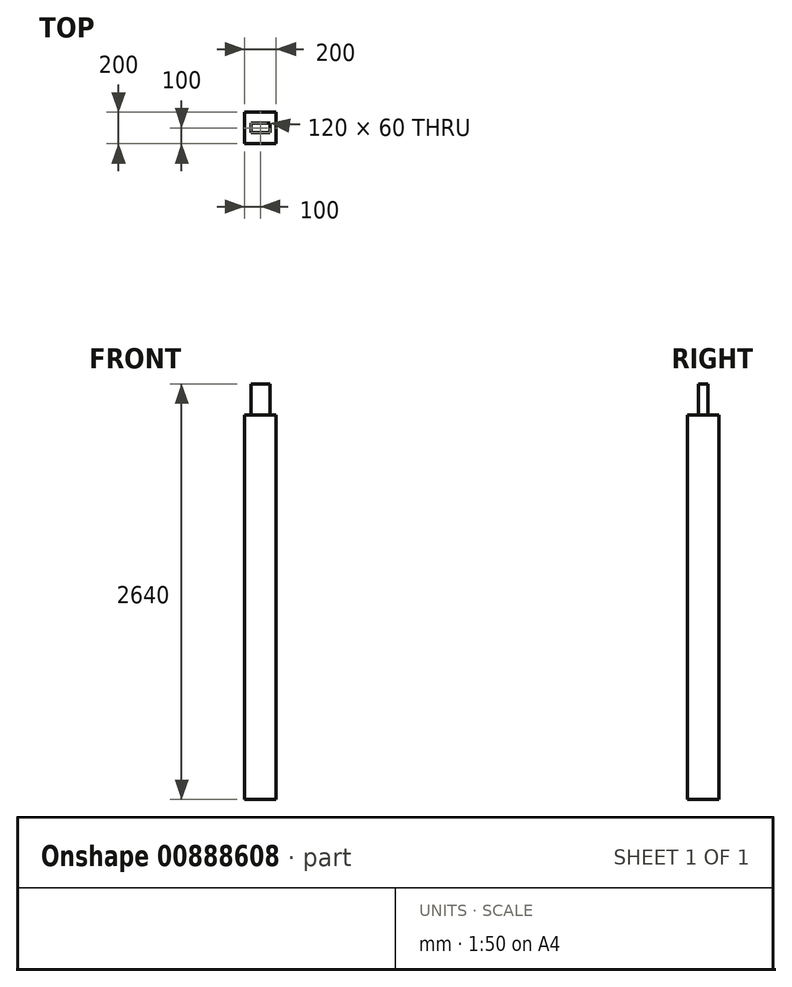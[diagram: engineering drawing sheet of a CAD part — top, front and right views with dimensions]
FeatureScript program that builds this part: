
annotation { "Feature Type Name" : "Feature", "Feature Type Description" : "" }
export const myFeature = defineFeature(function(context is Context, id is Id, definition is map)
    precondition{}
    {
        {
            var Q0;
            Q0=qCreatedBy(makeId("Top.planeOp"),FACE);
            var sketch = newSketch(context, id + "F0", { "sketchPlane" : qUnion([Q0])});
            skLineSegment(sketch, "E0.bottom", {"start": v(0, 0) * mm, "end": v(200, 0) * mm});
            skLineSegment(sketch, "E0.top", {"start": v(0, 200) * mm, "end": v(200, 200) * mm});
            skLineSegment(sketch, "E0.left", {"start": v(0, 0) * mm, "end": v(0, 200) * mm});
            skLineSegment(sketch, "E0.right", {"start": v(200, 0) * mm, "end": v(200, 200) * mm});
            skSolve(sketch);
        }
        {
            var Q0;
            Q0=makeQuery(id+"F0.imprint","IMPRINT",FACE,{"disambiguationData":[TD([[makeQuery(id+"F0.imprint","IMPRINT",EDGE,{"derivedFrom":sQuery(id+"F0.wireOp",EDGE,"E0.bottom")}),1.0]])]});
            extrude(context, id + "F1", {"entities" : qUnion([Q0]), "depth" : 2640 * mm, "offsetDistance" : 25 * mm});
        }
        {
            var Q0;
            Q0=makeQuery(id+"F1.opExtrude","CAP_FACE",FACE,{"disambiguationData":[OSD([sQuery(id+"F0.wireOp",EDGE,"E0.bottom"),sQuery(id+"F0.wireOp",EDGE,"E0.top"),sQuery(id+"F0.wireOp",EDGE,"E0.left"),sQuery(id+"F0.wireOp",EDGE,"E0.right")])],"isStart":false});
            var sketch = newSketch(context, id + "F2", { "sketchPlane" : qUnion([Q0])});
            skLineSegment(sketch, "E1.bottom", {"start": v(0, 0) * mm, "end": v(200, 0) * mm});
            skLineSegment(sketch, "E1.top", {"start": v(0, 200) * mm, "end": v(200, 200) * mm});
            skLineSegment(sketch, "E1.left", {"start": v(0, 0) * mm, "end": v(0, 200) * mm});
            skLineSegment(sketch, "E1.right", {"start": v(200, 0) * mm, "end": v(200, 200) * mm});
            skLineSegment(sketch, "E2.bottom", {"start": v(160, 70) * mm, "end": v(40, 70) * mm});
            skLineSegment(sketch, "E2.top", {"start": v(160, 130) * mm, "end": v(40, 130) * mm});
            skLineSegment(sketch, "E2.left", {"start": v(160, 70) * mm, "end": v(160, 130) * mm});
            skLineSegment(sketch, "E2.right", {"start": v(40, 70) * mm, "end": v(40, 130) * mm});
            skLineSegment(sketch, "E3", {"start": v(200, 100) * mm, "end": v(0, 100) * mm, "construction": true});
            skPoint(sketch, "E3.endSnap0", {"position": v(40, 100) * mm});
            skLineSegment(sketch, "E4", {"start": v(100, 0) * mm, "end": v(100, 200) * mm, "construction": true});
            skPoint(sketch, "E4.endSnap0", {"position": v(100, 70) * mm});
            skSolve(sketch);
        }
        {
            var Q0;
            Q0=makeQuery(id+"F2.imprint","IMPRINT",FACE,{"disambiguationData":[TD([[makeQuery(id+"F2.imprint","IMPRINT",EDGE,{"derivedFrom":sQuery(id+"F2.wireOp",EDGE,"E1.bottom")}),1.0]])]});
            extrude(context, id + "F3", {"entities" : qUnion([Q0]), "operationType" : NewBodyOperationType.REMOVE, "oppositeDirection" : true, "depth" : 200 * mm, "offsetDistance" : 25 * mm});
        }
    });
